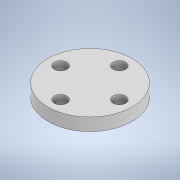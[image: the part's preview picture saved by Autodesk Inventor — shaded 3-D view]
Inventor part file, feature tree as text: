
AUTODESK INVENTOR PART (.ipt)
format: ipt  version: 2022 (Build 260153000, 153)  size: 107,008 bytes
history: native  units: mm
features: extrude x1, sketch x1
ambient origin geometry x8: Origin, YZ Plane, XZ Plane, XY Plane, X Axis, Y Axis, Z Axis, Center Point
bodies: Solid1 (feature_tree)
feature tree (2):
  extrude  "Extrusion1"  Depth=3.0mm
  sketch  "Sketch1"  dims[d0=20.0mm d1=13.97mm d2=3.0mm d3=40.0mm d5=360.0deg d7=3.0mm d8=0.0mm]
